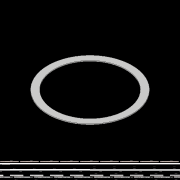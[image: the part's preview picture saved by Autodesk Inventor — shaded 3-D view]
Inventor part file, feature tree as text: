
AUTODESK INVENTOR PART (.ipt)
format: ipt  version: 2017 (Build 210142000, 142)  size: 101,888 bytes
history: native  units: in
note: dims shown in document units (in); Inventor stores cm internally (conversion verified against a paired STEP export)
features: extrude x2, sketch x2
ambient origin geometry x8: Origin, YZ Plane, XZ Plane, XY Plane, X Axis, Y Axis, Z Axis, Center Point
bodies: Solid1 (feature_tree)
feature tree (4):
  extrude  "Extrusion1"  Depth=0.125in TaperAngle=0.0deg
  extrude  "Extrusion2"  Depth=0.125in TaperAngle=0.0deg
  sketch  "Sketch1"  dims[d0=13.272in d1=0.125in d2=0.0in]
  sketch  "Sketch2"  dims[d3=11.25in d4=0.125in d5=0.0in]
